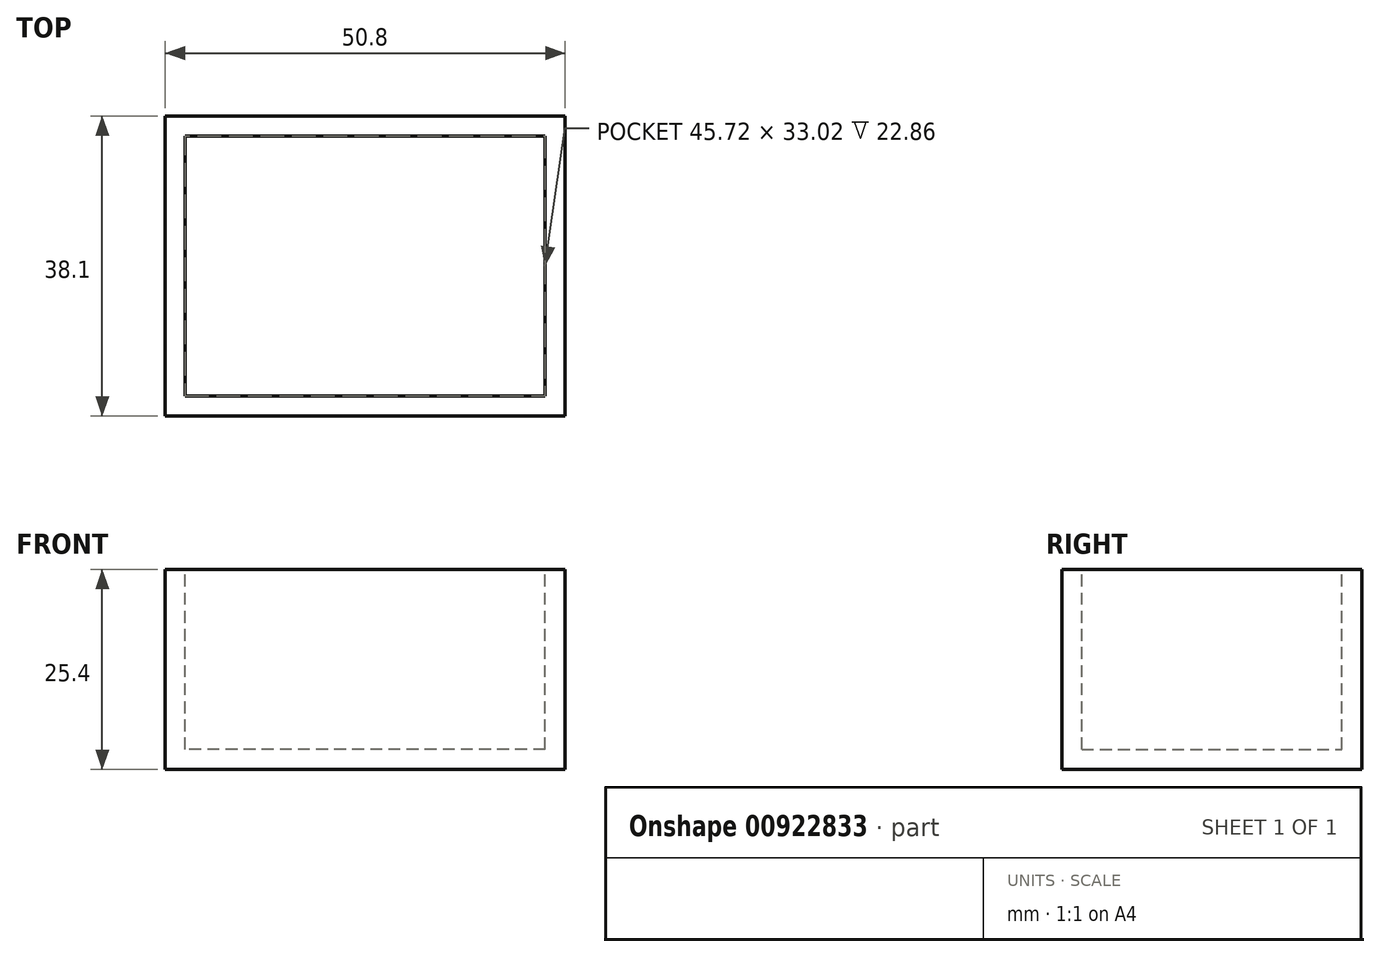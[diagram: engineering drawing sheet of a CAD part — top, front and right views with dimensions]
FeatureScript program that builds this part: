
annotation { "Feature Type Name" : "Feature", "Feature Type Description" : "" }
export const myFeature = defineFeature(function(context is Context, id is Id, definition is map)
    precondition{}
    {
        {
            var Q0;
            Q0=qCreatedBy(makeId("Top.planeOp"),FACE);
            var sketch = newSketch(context, id + "F0", { "sketchPlane" : qUnion([Q0])});
            skLineSegment(sketch, "E0.bottom", {"start": v(-63.85, 50.3) * mm, "end": v(-13.05, 50.3) * mm});
            skLineSegment(sketch, "E0.top", {"start": v(-63.85, 12.2) * mm, "end": v(-13.05, 12.2) * mm});
            skLineSegment(sketch, "E0.left", {"start": v(-63.85, 50.3) * mm, "end": v(-63.85, 12.2) * mm});
            skLineSegment(sketch, "E0.right", {"start": v(-13.05, 50.3) * mm, "end": v(-13.05, 12.2) * mm});
            skSolve(sketch);
        }
        {
            var Q0;
            Q0=makeQuery(id+"F0.imprint","IMPRINT",FACE,{"disambiguationData":[TD([[makeQuery(id+"F0.imprint","IMPRINT",EDGE,{"derivedFrom":sQuery(id+"F0.wireOp",EDGE,"E0.bottom")}),-1.0]])]});
            extrude(context, id + "F1", {"entities" : qUnion([Q0]), "depth" : 25.4 * mm, "offsetDistance" : 25.4 * mm});
        }
        {
            var Q0;
            Q0=makeQuery(id+"F1.opExtrude","CAP_FACE",FACE,{"disambiguationData":[OSD([sQuery(id+"F0.wireOp",EDGE,"E0.bottom"),sQuery(id+"F0.wireOp",EDGE,"E0.top"),sQuery(id+"F0.wireOp",EDGE,"E0.left"),sQuery(id+"F0.wireOp",EDGE,"E0.right")])],"isStart":false});
            var sketch = newSketch(context, id + "F2", { "sketchPlane" : qUnion([Q0])});
            skPoint(sketch, "E1", {"position": v(-38.45, 31.25) * mm});
            skPoint(sketch, "E1.positionSnap0", {"position": v(-63.85, 31.25) * mm});
            skPoint(sketch, "E1.positionSnap1", {"position": v(-38.45, 50.3) * mm});
            skLineSegment(sketch, "E2.bottom", {"start": v(-15.59, 14.74) * mm, "end": v(-61.3, 14.74) * mm});
            skLineSegment(sketch, "E2.top", {"start": v(-15.59, 47.76) * mm, "end": v(-61.3, 47.76) * mm});
            skLineSegment(sketch, "E2.left", {"start": v(-15.59, 14.74) * mm, "end": v(-15.59, 47.76) * mm});
            skLineSegment(sketch, "E2.right", {"start": v(-61.3, 14.74) * mm, "end": v(-61.3, 47.76) * mm});
            skSolve(sketch);
        }
        {
            var Q0;
            Q0=makeQuery(id+"F2.imprint","IMPRINT",FACE,{"disambiguationData":[TD([[makeQuery(id+"F2.imprint","IMPRINT",EDGE,{"derivedFrom":sQuery(id+"F2.wireOp",EDGE,"E2.bottom")}),-1.0]])]});
            extrude(context, id + "F3", {"entities" : qUnion([Q0]), "operationType" : NewBodyOperationType.REMOVE, "oppositeDirection" : true, "depth" : 22.86 * mm, "offsetDistance" : 25.4 * mm});
        }
    });
